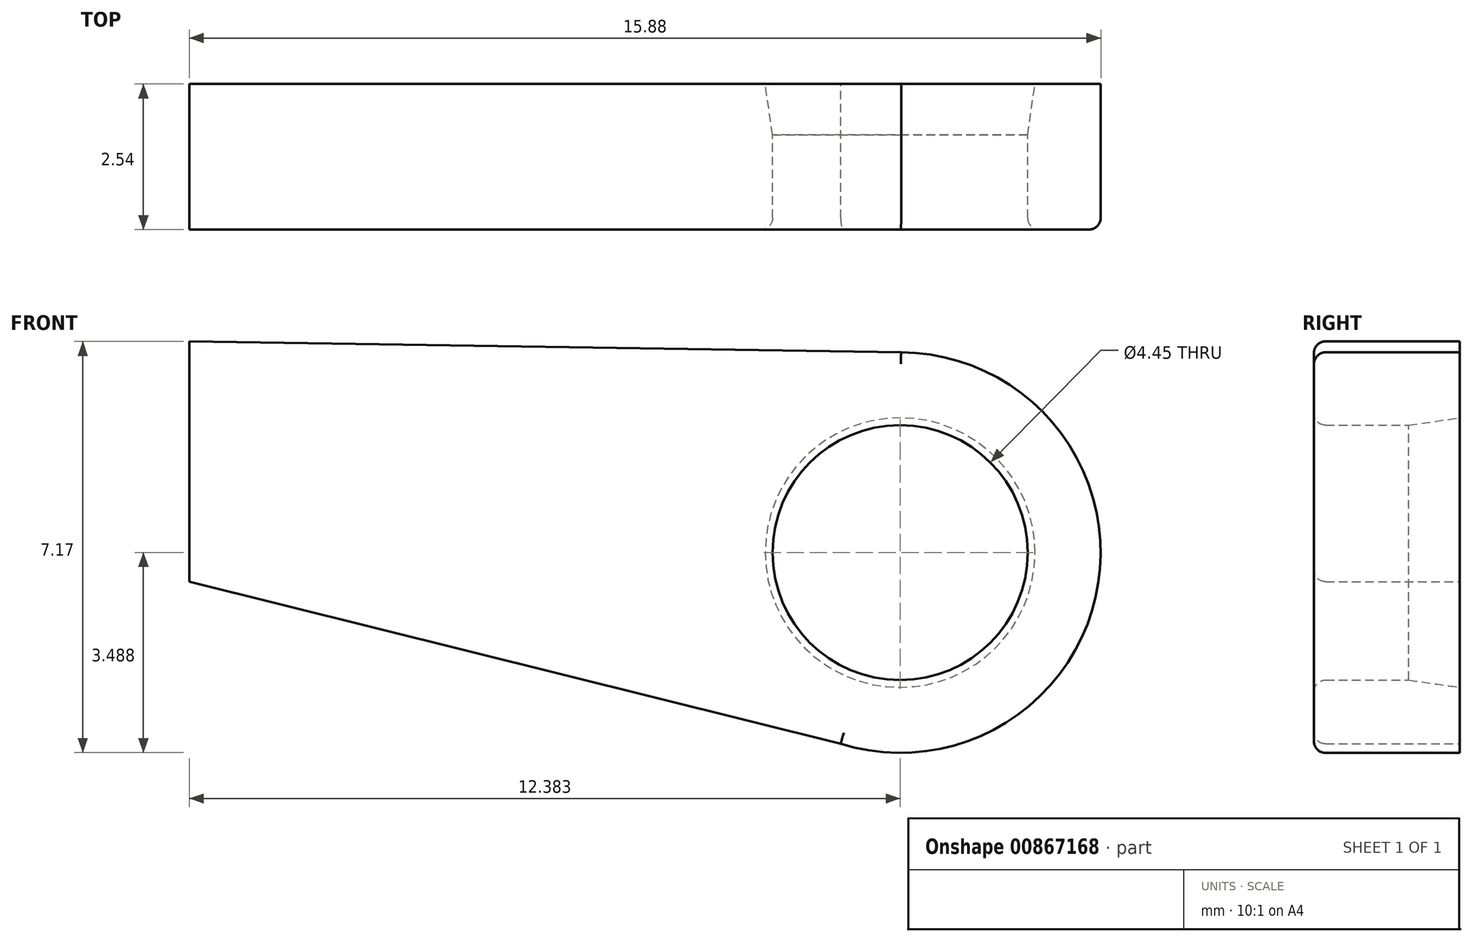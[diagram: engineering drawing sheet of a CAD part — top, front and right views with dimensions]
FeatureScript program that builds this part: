
annotation { "Feature Type Name" : "Feature", "Feature Type Description" : "" }
export const myFeature = defineFeature(function(context is Context, id is Id, definition is map)
    precondition{}
    {
        {
            var Q0;
            Q0=qCreatedBy(makeId("Front.planeOp"),FACE);
            var sketch = newSketch(context, id + "F0", { "sketchPlane" : qUnion([Q0])});
            skLineSegment(sketch, "E0", {"start": v(0, 0) * mm, "end": v(0, 4.2) * mm});
            skCircle(sketch, "E1", {"center": v(12.38, 0.5) * mm, "radius": 2.22 * mm});
            skArc(sketch, "E2.0", {"start": v(11.35, -2.83) * mm, "mid": v(15.83, -0.02) * mm, "end": v(12.4, 4) * mm});
            skLineSegment(sketch, "E3", {"start": v(12.47, 4) * mm, "end": v(0, 4.2) * mm});
            skLineSegment(sketch, "E4", {"start": v(11.35, -2.83) * mm, "end": v(0, 0) * mm});
            skPoint(sketch, "E5.end.orphan", {"position": v(0, -2.16) * mm});
            skSolve(sketch);
        }
        {
            var Q0;
            Q0 = qSketchRegion(id + "F0", true);
            extrude(context, id + "F1", {"entities" : qUnion([Q0]), "depth" : 2.54 * mm, "offsetDistance" : 25.4 * mm});
        }
        {
            var Q0;
            Q0=makeQuery(id+"F1.opExtrude","CAP_EDGE",EDGE,{"disambiguationData":[OSD([sQuery(id+"F0.wireOp",EDGE,"E2.0")])],"isStart":false});
            var Q1;
            Q1=makeQuery(id+"F1.opExtrude","CAP_EDGE",EDGE,{"disambiguationData":[OSD([sQuery(id+"F0.wireOp",EDGE,"E3")])],"isStart":false});
            var Q2;
            Q2=makeQuery(id+"F1.opExtrude","CAP_EDGE",EDGE,{"disambiguationData":[OSD([sQuery(id+"F0.wireOp",EDGE,"E4")])],"isStart":false});
            var Q3;
            Q3=makeQuery(id+"F1.opExtrude","CAP_EDGE",EDGE,{"disambiguationData":[OSD([sQuery(id+"F0.wireOp",EDGE,"E1")])],"isStart":false});
            fillet(context, id + "F2", {"entities" : qUnion([Q0, Q1, Q2, Q3]), "radius" : 0.2 * mm, "tangentPropagation" : true, "allowEdgeOverflow" : false});
        }
        {
            var Q0;
            Q0=makeQuery(id+"F1.opExtrude","CAP_EDGE",EDGE,{"disambiguationData":[OSD([sQuery(id+"F0.wireOp",EDGE,"E1")])],"isStart":true});
            chamfer(context, id + "F3", {"entities" : qUnion([Q0]), "chamferType" : ChamferType.TWO_OFFSETS, "width1" : 0.13 * mm, "oppositeDirection" : false, "width2" : 0.89 * mm, "tangentPropagation" : true});
        }
    });
